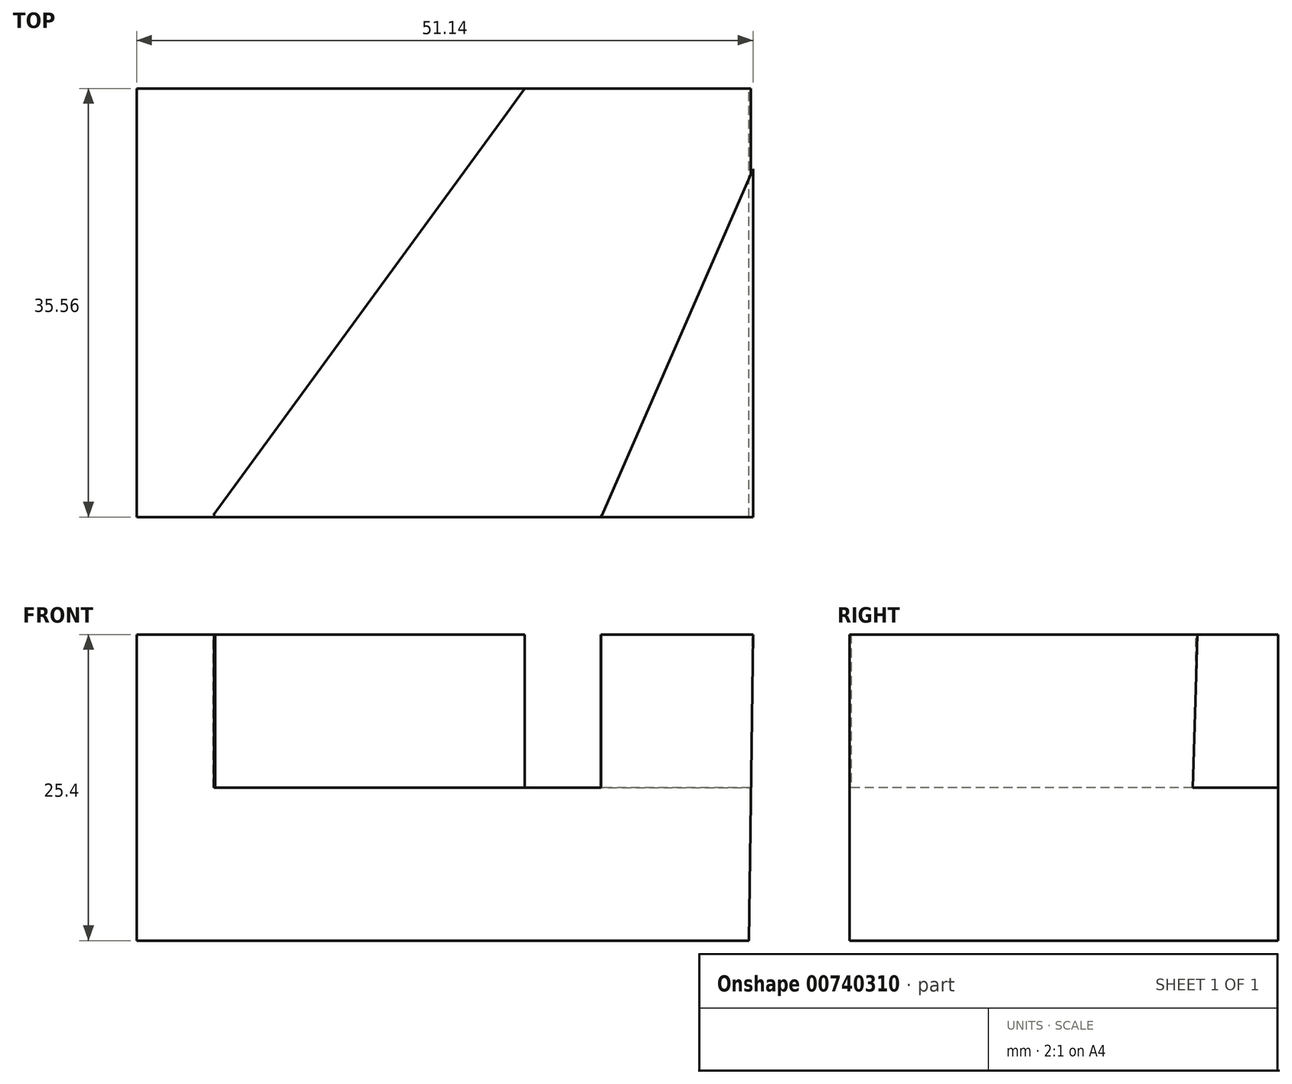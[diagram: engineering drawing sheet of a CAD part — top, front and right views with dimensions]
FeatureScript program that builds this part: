
annotation { "Feature Type Name" : "Feature", "Feature Type Description" : "" }
export const myFeature = defineFeature(function(context is Context, id is Id, definition is map)
    precondition{}
    {
        {
            var Q0;
            Q0=qCreatedBy(makeId("Front.planeOp"),FACE);
            var sketch = newSketch(context, id + "F0", { "sketchPlane" : qUnion([Q0])});
            skLineSegment(sketch, "E0", {"start": v(0, 0) * mm, "end": v(50.8, 0) * mm});
            skLineSegment(sketch, "E1", {"start": v(50.8, 0) * mm, "end": v(51.14, 25.4) * mm});
            skLineSegment(sketch, "E2", {"start": v(51.14, 25.4) * mm, "end": v(0, 25.4) * mm});
            skLineSegment(sketch, "E3", {"start": v(0, 25.4) * mm, "end": v(0, 0) * mm});
            skSolve(sketch);
        }
        {
            var Q0;
            Q0 = qSketchRegion(id + "F0", true);
            extrude(context, id + "F1", {"entities" : qUnion([Q0]), "depth" : 35.56 * mm, "offsetDistance" : 25.4 * mm});
        }
        {
            var Q0;
            Q0=makeQuery(id+"F1.opExtrude","SWEPT_FACE",FACE,{"disambiguationData":[OSD([sQuery(id+"F0.wireOp",EDGE,"E2")])]});
            var sketch = newSketch(context, id + "F2", { "sketchPlane" : qUnion([Q0])});
            skLineSegment(sketch, "E4", {"start": v(0, -35.56) * mm, "end": v(6.36, -35.56) * mm});
            skSolve(sketch);
        }
        {
            var Q0;
            {var subQ2=sQuery(id+"F2.wireOp",EDGE,"E4");Q0=makeQuery(id+"F2.imprint","IMPRINT",FACE,{"disambiguationData":[TD([[makeQuery(id+"F2.imprint","IMPRINT",EDGE,{"derivedFrom":subQ2}),-1.0]])]});}
            var sketch = newSketch(context, id + "F3", { "sketchPlane" : qUnion([Q0])});
            skLineSegment(sketch, "E5", {"start": v(32.21, 0) * mm, "end": v(51.2, 0) * mm});
            skLineSegment(sketch, "E6", {"start": v(51.2, 0) * mm, "end": v(51.2, -6.52) * mm});
            skLineSegment(sketch, "E7", {"start": v(51.2, -6.52) * mm, "end": v(38.51, -35.57) * mm});
            skLineSegment(sketch, "E8", {"start": v(38.51, -35.57) * mm, "end": v(6.42, -35.57) * mm});
            skLineSegment(sketch, "E9", {"start": v(6.42, -35.57) * mm, "end": v(32.21, 0) * mm});
            skSolve(sketch);
        }
        {
            var Q0;
            Q0 = qSketchRegion(id + "F3", true);
            extrude(context, id + "F4", {"entities" : qUnion([Q0]), "operationType" : NewBodyOperationType.REMOVE, "oppositeDirection" : true, "depth" : 12.7 * mm, "offsetDistance" : 25.4 * mm});
        }
        {
            var Q0;
            {var subQ2=sQuery(id+"F2.wireOp",EDGE,"E4");Q0=makeQuery(id+"F2.imprint","IMPRINT",FACE,{"disambiguationData":[TD([[makeQuery(id+"F2.imprint","IMPRINT",EDGE,{"derivedFrom":subQ2}),-1.0]])]});}
            var sketch = newSketch(context, id + "F5", { "sketchPlane" : qUnion([Q0])});
            skLineSegment(sketch, "E10", {"start": v(32.22, 0) * mm, "end": v(51.08, 0) * mm});
            skLineSegment(sketch, "E11", {"start": v(51.08, 0) * mm, "end": v(51.08, -6.83) * mm});
            skLineSegment(sketch, "E12", {"start": v(51.08, -6.83) * mm, "end": v(38.6, -35.43) * mm});
            skLineSegment(sketch, "E13", {"start": v(38.6, -35.43) * mm, "end": v(6.35, -35.43) * mm});
            skLineSegment(sketch, "E14", {"start": v(6.35, -35.43) * mm, "end": v(32.22, 0) * mm});
            skLineSegment(sketch, "E15", {"start": v(51.08, 0) * mm, "end": v(32.22, 0) * mm});
            skSolve(sketch);
        }
        {
            var Q0;
            Q0=makeQuery(id+"F5.imprint","IMPRINT",FACE,{"disambiguationData":[TD([[makeQuery(id+"F5.imprint","IMPRINT",EDGE,{"derivedFrom":sQuery(id+"F5.wireOp",EDGE,"E11")}),-1.0]])]});
            extrude(context, id + "F6", {"entities" : qUnion([Q0]), "operationType" : NewBodyOperationType.REMOVE, "oppositeDirection" : true, "depth" : 12.7 * mm, "offsetDistance" : 25.4 * mm});
        }
        {
            var Q0;
            Q0 = qSketchRegion(id + "F5", true);
            extrude(context, id + "F7", {"entities" : qUnion([Q0]), "operationType" : NewBodyOperationType.REMOVE, "oppositeDirection" : true, "depth" : 12.7 * mm, "offsetDistance" : 25.4 * mm});
        }
    });
